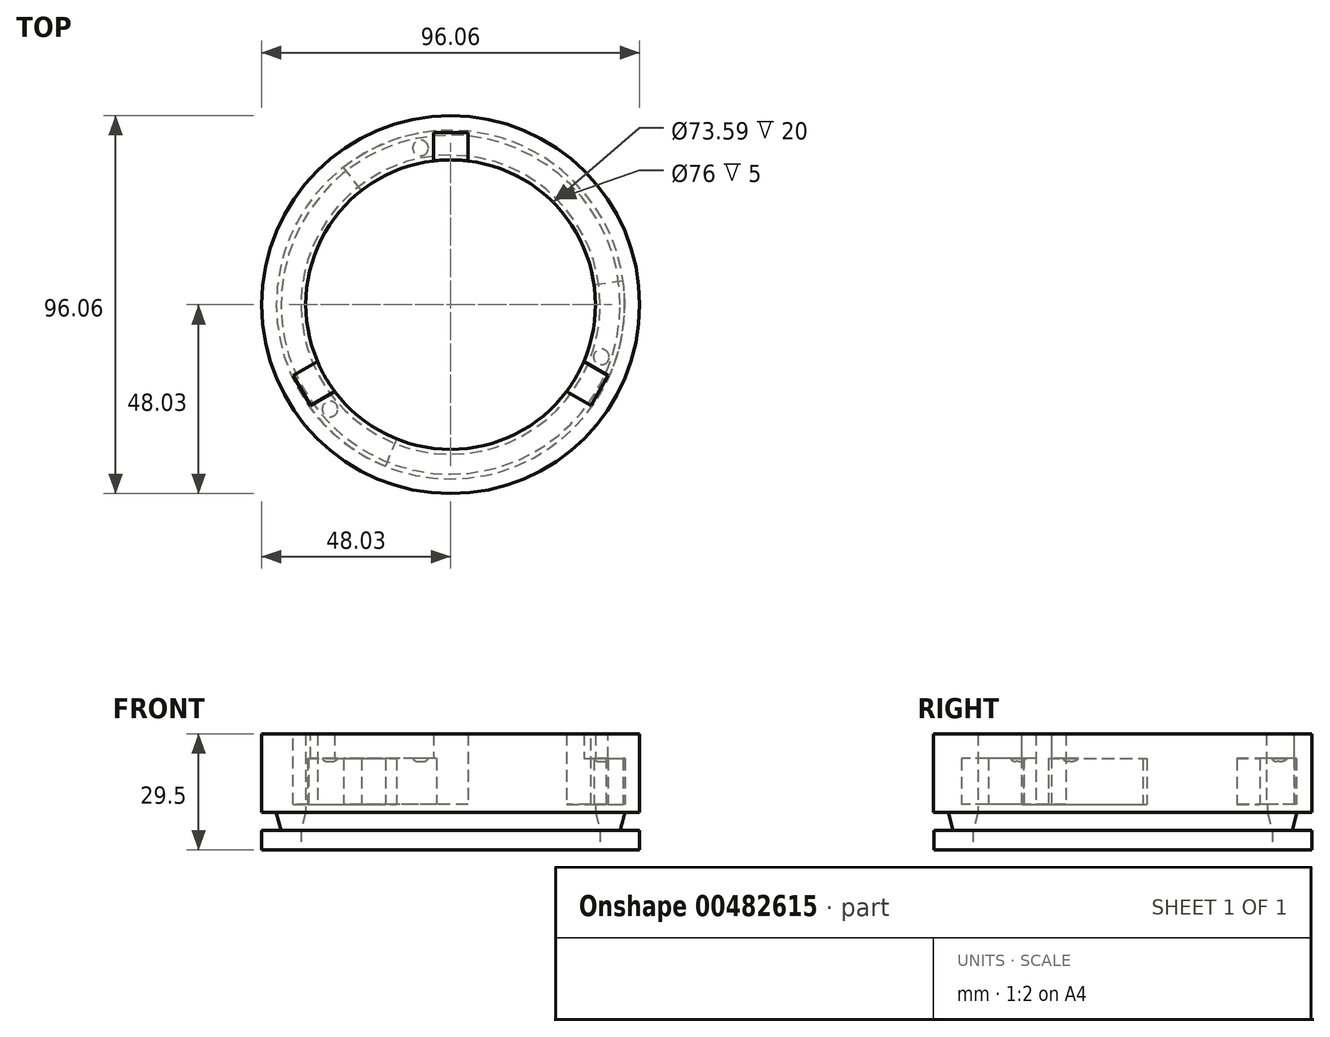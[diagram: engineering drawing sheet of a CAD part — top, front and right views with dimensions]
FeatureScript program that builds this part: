
annotation { "Feature Type Name" : "Feature", "Feature Type Description" : "" }
export const myFeature = defineFeature(function(context is Context, id is Id, definition is map)
    precondition{}
    {
        {
            var Q0;
            Q0=qCreatedBy(makeId("Top.planeOp"),FACE);
            var sketch = newSketch(context, id + "F0", { "sketchPlane" : qUnion([Q0])});
            skCircle(sketch, "E0", {"center": v(0, 0) * mm, "radius": 48 * mm});
            skCircle(sketch, "E1.0", {"center": v(0, 0) * mm, "radius": 42 * mm});
            skCircle(sketch, "E2", {"center": v(0, 0) * mm, "radius": 38 * mm});
            skSolve(sketch);
        }
        {
            var Q0;
            Q0=makeQuery(id+"F0.imprint","IMPRINT",FACE,{"disambiguationData":[TD([[makeQuery(id+"F0.imprint","IMPRINT",EDGE,{"derivedFrom":sQuery(id+"F0.wireOp",EDGE,"E0")}),1.0]])]});
            var Q1;
            Q1=makeQuery(id+"F0.imprint","IMPRINT",FACE,{"disambiguationData":[TD([[makeQuery(id+"F0.imprint","IMPRINT",EDGE,{"derivedFrom":sQuery(id+"F0.wireOp",EDGE,"E1.0")}),1.0]])]});
            extrude(context, id + "F1", {"entities" : qUnion([Q0, Q1]), "depth" : 5 * mm});
        }
        {
            var Q0;
            Q0=makeQuery(id+"F1.opExtrude","CAP_FACE",FACE,{"disambiguationData":[OSD([sQuery(id+"F0.wireOp",EDGE,"E0"),sQuery(id+"F0.wireOp",EDGE,"E2")])],"isStart":false});
            var sketch = newSketch(context, id + "F2", { "sketchPlane" : qUnion([Q0])});
            skCircle(sketch, "E3", {"center": v(0, 0) * mm, "radius": 43.08 * mm});
            skCircle(sketch, "E4.0", {"center": v(0, 0) * mm, "radius": 38 * mm});
            skSolve(sketch);
        }
        {
            var Q0;
            Q0=makeQuery(id+"F2.imprint","IMPRINT",FACE,{"disambiguationData":[TD([[makeQuery(id+"F2.imprint","IMPRINT",EDGE,{"derivedFrom":sQuery(id+"F2.wireOp",EDGE,"E3")}),1.0]])]});
            extrude(context, id + "F3", {"entities" : qUnion([Q0]), "operationType" : NewBodyOperationType.ADD, "depth" : 4.5 * mm, "hasDraft" : true, "draftAngle" : 15 * degree});
        }
        {
            var Q0;
            Q0=makeQuery(id+"F3.opExtrude","CAP_FACE",FACE,{"disambiguationData":[OSD([sQuery(id+"F2.wireOp",EDGE,"E3"),sQuery(id+"F2.wireOp",EDGE,"E4.0")])],"isStart":false});
            var sketch = newSketch(context, id + "F4", { "sketchPlane" : qUnion([Q0])});
            skCircle(sketch, "E5", {"center": v(0, 0) * mm, "radius": 48.03 * mm});
            skCircle(sketch, "E6", {"center": v(0, 0) * mm, "radius": 35.37 * mm});
            skSolve(sketch);
        }
        {
            var Q0;
            Q0=makeQuery(id+"F4.imprint","IMPRINT",FACE,{"disambiguationData":[TD([[makeQuery(id+"F4.imprint","IMPRINT",EDGE,{"derivedFrom":makeQuery(id+"F3.opExtrude","CAP_EDGE",EDGE,{"disambiguationData":[OSD([sQuery(id+"F2.wireOp",EDGE,"E3")])],"isStart":false})}),1.0]])]});
            var Q1;
            Q1=makeQuery(id+"F4.imprint","IMPRINT",FACE,{"disambiguationData":[TD([[makeQuery(id+"F4.imprint","IMPRINT",EDGE,{"derivedFrom":sQuery(id+"F4.wireOp",EDGE,"E5")}),1.0]])]});
            extrude(context, id + "F5", {"entities" : qUnion([Q0, Q1]), "operationType" : NewBodyOperationType.ADD, "depth" : 20 * mm});
        }
        {
            var Q0;
            Q0=makeQuery(id+"F5.opExtrude","CAP_FACE",FACE,{"disambiguationData":[OSD([sQuery(id+"F2.wireOp",EDGE,"E4.0"),sQuery(id+"F4.wireOp",EDGE,"E5")])],"isStart":false});
            var sketch = newSketch(context, id + "F6", { "sketchPlane" : qUnion([Q0])});
            skPoint(sketch, "E7", {"position": v(0, 0) * mm});
            skLineSegment(sketch, "E8", {"start": v(0, 0) * mm, "end": v(0, 82.96) * mm, "construction": true});
            skCircle(sketch, "E9", {"center": v(0, 0) * mm, "radius": 38.33 * mm, "construction": true});
            skLineSegment(sketch, "E10", {"start": v(0, 43.66) * mm, "end": v(-4.39, 43.66) * mm});
            skLineSegment(sketch, "E11", {"start": v(-4.39, 43.66) * mm, "end": v(-4.39, 34.06) * mm});
            skLineSegment(sketch, "E12", {"start": v(-4.39, 34.06) * mm, "end": v(0, 34.06) * mm});
            skLineSegment(sketch, "E13.MirrorCS", {"start": v(0, 43.66) * mm, "end": v(4.39, 43.66) * mm});
            skLineSegment(sketch, "E14.MirrorCS", {"start": v(4.39, 43.66) * mm, "end": v(4.39, 34.06) * mm});
            skLineSegment(sketch, "E15.MirrorCS", {"start": v(4.39, 34.06) * mm, "end": v(0, 34.06) * mm});
            skLineSegment(sketch, "E16.1.0", {"start": v(-27.3, -20.83) * mm, "end": v(-29.5, -17.03) * mm});
            skLineSegment(sketch, "E16.1.1", {"start": v(-37.81, -21.83) * mm, "end": v(-40, -18.03) * mm});
            skLineSegment(sketch, "E16.1.2", {"start": v(-35.62, -25.63) * mm, "end": v(-27.3, -20.83) * mm});
            skLineSegment(sketch, "E16.1.3", {"start": v(-31.69, -13.23) * mm, "end": v(-29.5, -17.03) * mm});
            skLineSegment(sketch, "E16.1.4", {"start": v(-40, -18.03) * mm, "end": v(-31.69, -13.23) * mm});
            skLineSegment(sketch, "E16.1.5", {"start": v(-37.81, -21.83) * mm, "end": v(-35.62, -25.63) * mm});
            skLineSegment(sketch, "E16.1.6", {"start": v(0, 0) * mm, "end": v(-71.84, -41.48) * mm, "construction": true});
            skLineSegment(sketch, "E16.2.0", {"start": v(31.69, -13.23) * mm, "end": v(29.5, -17.03) * mm});
            skLineSegment(sketch, "E16.2.1", {"start": v(37.81, -21.83) * mm, "end": v(35.62, -25.63) * mm});
            skLineSegment(sketch, "E16.2.2", {"start": v(40, -18.03) * mm, "end": v(31.69, -13.23) * mm});
            skLineSegment(sketch, "E16.2.3", {"start": v(27.3, -20.83) * mm, "end": v(29.5, -17.03) * mm});
            skLineSegment(sketch, "E16.2.4", {"start": v(35.62, -25.63) * mm, "end": v(27.3, -20.83) * mm});
            skLineSegment(sketch, "E16.2.5", {"start": v(37.81, -21.83) * mm, "end": v(40, -18.03) * mm});
            skLineSegment(sketch, "E16.2.6", {"start": v(0, 0) * mm, "end": v(71.84, -41.48) * mm, "construction": true});
            skSolve(sketch);
        }
        {
            var Q0;
            Q0 = qSketchRegion(id + "F6", true);
            extrude(context, id + "F7", {"entities" : qUnion([Q0]), "operationType" : NewBodyOperationType.REMOVE, "oppositeDirection" : true, "depth" : 18 * mm});
        }
        {
            var Q0;
            Q0=makeQuery(id+"F7.boolean.opBoolean","COPY",FACE,{"derivedFrom":makeQuery(id+"F7.opExtrude","CAP_FACE",FACE,{"disambiguationData":[OSD([sQuery(id+"F6.wireOp",EDGE,"E10"),sQuery(id+"F6.wireOp",EDGE,"E11"),sQuery(id+"F6.wireOp",EDGE,"E12"),sQuery(id+"F6.wireOp",EDGE,"E13.MirrorCS"),sQuery(id+"F6.wireOp",EDGE,"E14.MirrorCS"),sQuery(id+"F6.wireOp",EDGE,"E15.MirrorCS")])],"isStart":false})});
            var sketch = newSketch(context, id + "F8", { "sketchPlane" : qUnion([Q0])});
            skCircle(sketch, "E17.0", {"center": v(0, 0) * mm, "radius": 36.8 * mm});
            skArc(sketch, "E18", {"start": v(-36.39, -25.16) * mm, "mid": v(-27.65, -34.53) * mm, "end": v(-16.59, -41.01) * mm});
            skLineSegment(sketch, "E19", {"start": v(-3.6, 44.1) * mm, "end": v(-3.6, 33.31) * mm});
            skLineSegment(sketch, "E20", {"start": v(-3.6, 33.31) * mm, "end": v(-20.26, 25.86) * mm});
            skLineSegment(sketch, "E21", {"start": v(-20.26, 25.86) * mm, "end": v(-27.22, 34.87) * mm});
            skLineSegment(sketch, "E22.1.0", {"start": v(-12.27, -30.47) * mm, "end": v(-16.59, -41.01) * mm});
            skLineSegment(sketch, "E22.1.1", {"start": v(-27.06, -19.77) * mm, "end": v(-12.27, -30.47) * mm});
            skLineSegment(sketch, "E22.1.2", {"start": v(-36.39, -25.16) * mm, "end": v(-27.06, -19.77) * mm});
            skLineSegment(sketch, "E22.2.0", {"start": v(32.53, 4.61) * mm, "end": v(43.8, 6.14) * mm});
            skLineSegment(sketch, "E22.2.1", {"start": v(30.65, -13.55) * mm, "end": v(32.53, 4.61) * mm});
            skLineSegment(sketch, "E22.2.2", {"start": v(39.98, -18.93) * mm, "end": v(30.65, -13.55) * mm});
            skArc(sketch, "E23.trimOffspring", {"start": v(-3.6, 44.1) * mm, "mid": v(-16.08, 41.21) * mm, "end": v(-27.22, 34.87) * mm});
            skArc(sketch, "E24.trimOffspring", {"start": v(39.98, -18.93) * mm, "mid": v(43.73, -6.68) * mm, "end": v(43.8, 6.14) * mm});
            skCircle(sketch, "E25", {"center": v(0, 0) * mm, "radius": 44.24 * mm, "construction": true});
            skSolve(sketch);
        }
        {
            var Q0;
            {var subQ0=sQuery(id+"F8.wireOp",EDGE,"E23.trimOffspring");Q0=makeQuery(id+"F8.imprint","IMPRINT",FACE,{"disambiguationData":[TD([[makeQuery(id+"F8.imprint","IMPRINT",EDGE,{"derivedFrom":subQ0}),1.0]])]});}
            var Q1;
            {var subQ5=sQuery(id+"F8.wireOp",EDGE,"E24.trimOffspring");Q1=makeQuery(id+"F8.imprint","IMPRINT",FACE,{"disambiguationData":[TD([[makeQuery(id+"F8.imprint","IMPRINT",EDGE,{"derivedFrom":subQ5}),1.0]])]});}
            var Q2;
            {var subQ5=sQuery(id+"F8.wireOp",EDGE,"E18");Q2=makeQuery(id+"F8.imprint","IMPRINT",FACE,{"disambiguationData":[TD([[makeQuery(id+"F8.imprint","IMPRINT",EDGE,{"derivedFrom":subQ5}),1.0]])]});}
            extrude(context, id + "F9", {"entities" : qUnion([Q0, Q1, Q2]), "operationType" : NewBodyOperationType.REMOVE, "depth" : 11.7 * mm});
        }
        {
            var Q0;
            Q0=makeQuery(id+"F9.boolean.opBoolean","COPY",FACE,{"derivedFrom":makeQuery(id+"F9.opExtrude","CAP_FACE",FACE,{"disambiguationData":[OSD([sQuery(id+"F8.wireOp",EDGE,"E17.0"),sQuery(id+"F8.wireOp",EDGE,"E18"),sQuery(id+"F8.wireOp",EDGE,"E22.1.0"),sQuery(id+"F8.wireOp",EDGE,"E22.1.2")])],"isStart":false})});
            var sketch = newSketch(context, id + "F10", { "sketchPlane" : qUnion([Q0])});
            skCircle(sketch, "E26", {"center": v(-30.64, 26.52) * mm, "radius": 1.99 * mm});
            skCircle(sketch, "E27.1.0", {"center": v(-7.64, -39.8) * mm, "radius": 1.99 * mm});
            skCircle(sketch, "E27.2.0", {"center": v(38.29, 13.28) * mm, "radius": 1.99 * mm});
            skPoint(sketch, "E27.center", {"position": v(0, 0) * mm});
            skSolve(sketch);
        }
        {
            var Q0;
            Q0=makeQuery(id+"F10.imprint","IMPRINT",FACE,{"disambiguationData":[TD([[makeQuery(id+"F10.imprint","IMPRINT",EDGE,{"derivedFrom":sQuery(id+"F10.wireOp",EDGE,"E26")}),1.0]])]});
            var Q1;
            Q1=makeQuery(id+"F10.imprint","IMPRINT",FACE,{"disambiguationData":[TD([[makeQuery(id+"F10.imprint","IMPRINT",EDGE,{"derivedFrom":sQuery(id+"F10.wireOp",EDGE,"E27.2.0")}),1.0]])]});
            var Q2;
            Q2=makeQuery(id+"F10.imprint","IMPRINT",FACE,{"disambiguationData":[TD([[makeQuery(id+"F10.imprint","IMPRINT",EDGE,{"derivedFrom":sQuery(id+"F10.wireOp",EDGE,"E27.1.0")}),1.0]])]});
            extrude(context, id + "F11", {"entities" : qUnion([Q0, Q1, Q2]), "operationType" : NewBodyOperationType.ADD, "depth" : 0.73 * mm});
        }
        {
            var Q0;
            Q0=makeQuery(id+"F11.opExtrude","CAP_EDGE",EDGE,{"disambiguationData":[OSD([sQuery(id+"F10.wireOp",EDGE,"E26")])],"isStart":false});
            var Q1;
            Q1=makeQuery(id+"F11.opExtrude","CAP_EDGE",EDGE,{"disambiguationData":[OSD([sQuery(id+"F10.wireOp",EDGE,"E27.2.0")])],"isStart":false});
            var Q2;
            Q2=makeQuery(id+"F11.opExtrude","CAP_EDGE",EDGE,{"disambiguationData":[OSD([sQuery(id+"F10.wireOp",EDGE,"E27.1.0")])],"isStart":false});
            fillet(context, id + "F12", {"entities" : qUnion([Q0, Q1, Q2]), "radius" : 1.69 * mm, "tangentPropagation" : true, "allowEdgeOverflow" : false});
        }
    });
